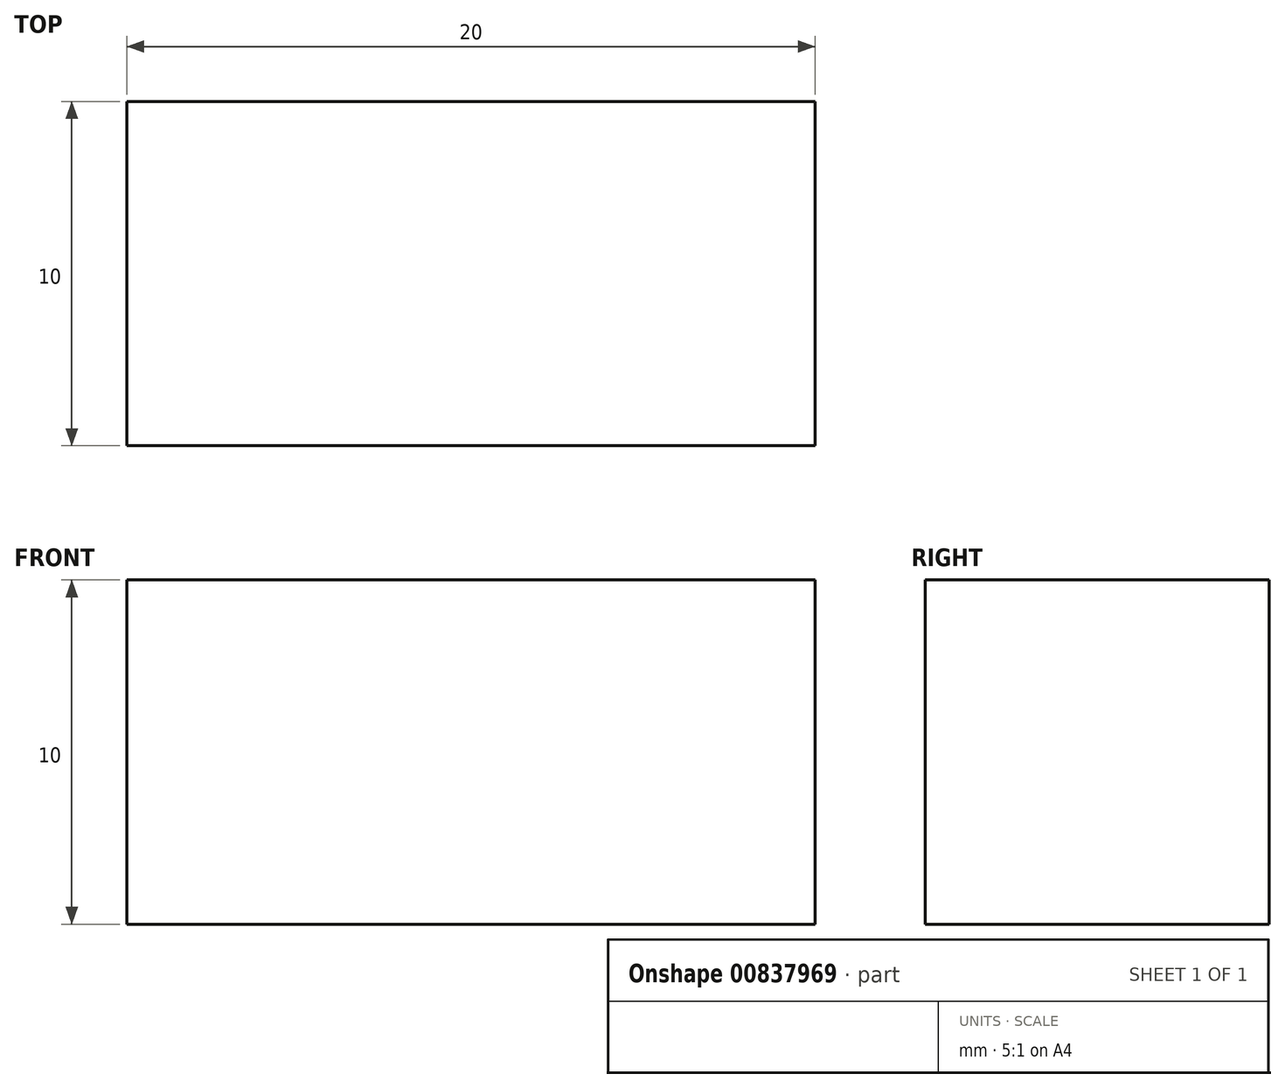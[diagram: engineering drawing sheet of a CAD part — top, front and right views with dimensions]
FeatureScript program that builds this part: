
annotation { "Feature Type Name" : "Feature", "Feature Type Description" : "" }
export const myFeature = defineFeature(function(context is Context, id is Id, definition is map)
    precondition{}
    {
        {
            var Q0;
            Q0=qCreatedBy(makeId("Top.planeOp"),FACE);
            var sketch = newSketch(context, id + "F0", { "sketchPlane" : qUnion([Q0])});
            skLineSegment(sketch, "E0.bottom", {"start": v(-31.2, -6.81) * mm, "end": v(-11.2, -6.81) * mm});
            skLineSegment(sketch, "E0.top", {"start": v(-31.2, -16.81) * mm, "end": v(-11.2, -16.81) * mm});
            skLineSegment(sketch, "E0.left", {"start": v(-31.2, -6.81) * mm, "end": v(-31.2, -16.81) * mm});
            skLineSegment(sketch, "E0.right", {"start": v(-11.2, -6.81) * mm, "end": v(-11.2, -16.81) * mm});
            skSolve(sketch);
        }
        {
            var Q0;
            Q0=makeQuery(id+"F0.imprint","IMPRINT",FACE,{"disambiguationData":[TD([[makeQuery(id+"F0.imprint","IMPRINT",EDGE,{"derivedFrom":sQuery(id+"F0.wireOp",EDGE,"E0.bottom")}),-1.0]])]});
            extrude(context, id + "F1", {"entities" : qUnion([Q0]), "depth" : 10 * mm, "offsetDistance" : 25 * mm});
        }
    });
